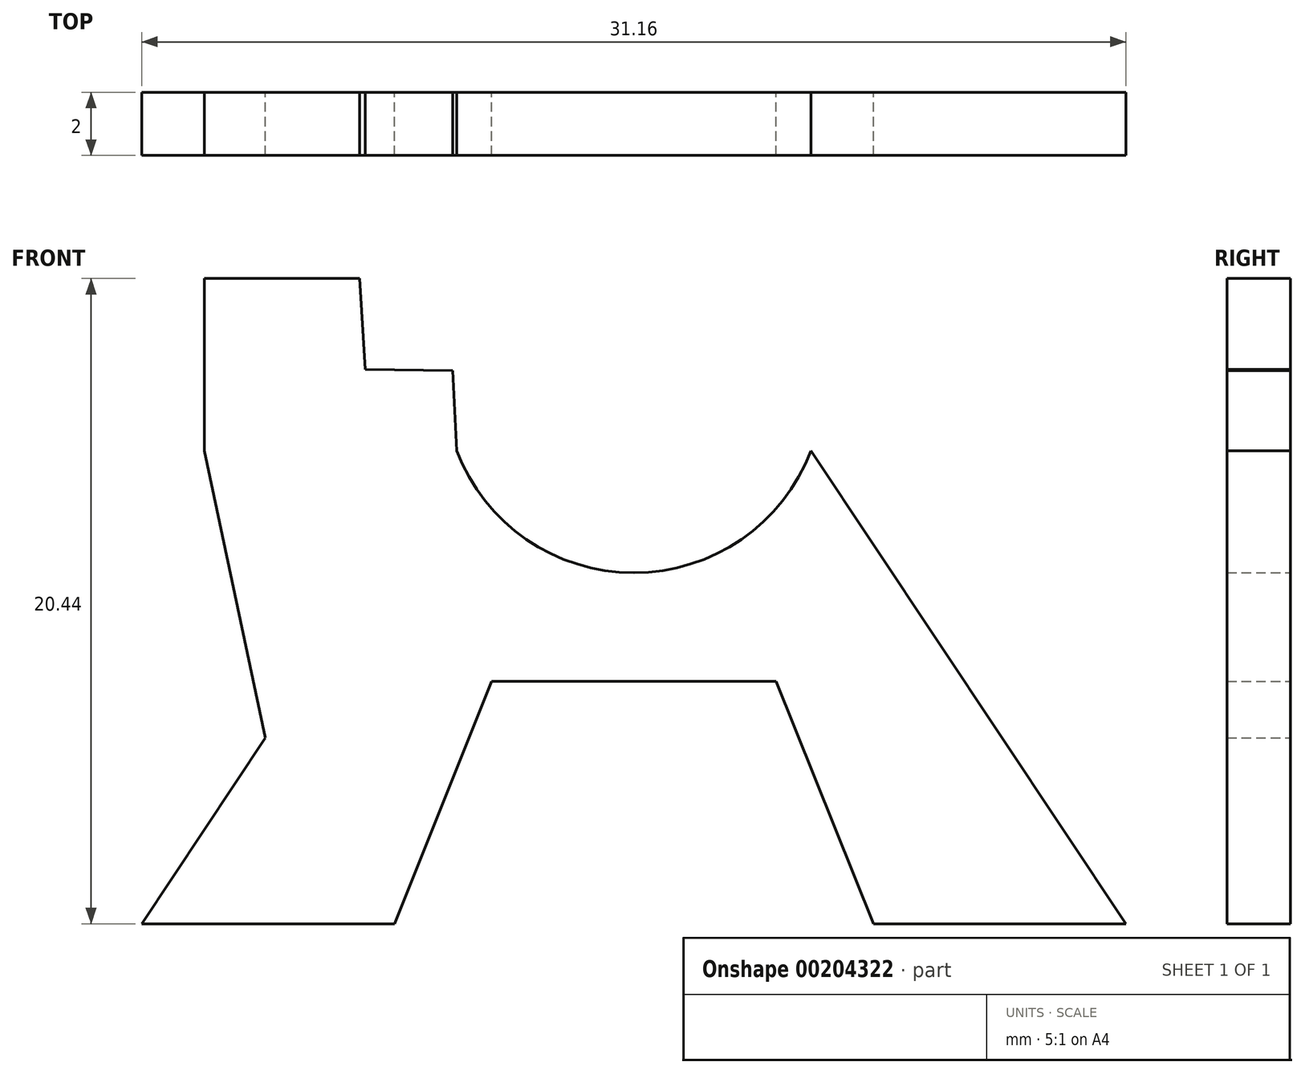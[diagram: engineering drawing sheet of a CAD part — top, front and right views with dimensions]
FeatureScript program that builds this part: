
annotation { "Feature Type Name" : "Feature", "Feature Type Description" : "" }
export const myFeature = defineFeature(function(context is Context, id is Id, definition is map)
    precondition{}
    {
        {
            var Q0;
            Q0=qCreatedBy(makeId("Front.planeOp"),FACE);
            var sketch = newSketch(context, id + "F0", { "sketchPlane" : qUnion([Q0])});
            skLineSegment(sketch, "E0", {"start": v(15.58, 0) * mm, "end": v(7.58, 0) * mm});
            skLineSegment(sketch, "E1", {"start": v(7.58, 0) * mm, "end": v(4.5, 7.68) * mm});
            skLineSegment(sketch, "E2", {"start": v(4.5, 7.68) * mm, "end": v(-4.5, 7.68) * mm});
            skLineSegment(sketch, "E3", {"start": v(-4.5, 7.68) * mm, "end": v(-7.58, 0) * mm});
            skLineSegment(sketch, "E4", {"start": v(-7.58, 0) * mm, "end": v(-15.58, 0) * mm});
            skLineSegment(sketch, "E5", {"start": v(0, 0) * mm, "end": v(0, 16.32) * mm, "construction": true});
            skArc(sketch, "E6", {"start": v(-5.6, 14.98) * mm, "mid": v(0, 11.12) * mm, "end": v(5.6, 14.98) * mm});
            skLineSegment(sketch, "E7", {"start": v(-15.58, 0) * mm, "end": v(-5.6, 14.98) * mm});
            skLineSegment(sketch, "E8", {"start": v(5.6, 14.98) * mm, "end": v(15.58, 0) * mm});
            skLineSegment(sketch, "E9", {"start": v(-13.6, 14.98) * mm, "end": v(-13.6, 20.44) * mm});
            skLineSegment(sketch, "E10", {"start": v(-13.6, 20.44) * mm, "end": v(-8.69, 20.44) * mm});
            skLineSegment(sketch, "E11", {"start": v(-8.69, 20.44) * mm, "end": v(-8.5, 17.56) * mm});
            skLineSegment(sketch, "E12", {"start": v(-8.5, 17.56) * mm, "end": v(-5.73, 17.52) * mm});
            skLineSegment(sketch, "E13", {"start": v(-5.73, 17.52) * mm, "end": v(-5.6, 14.98) * mm});
            skLineSegment(sketch, "E14", {"start": v(-13.6, 14.98) * mm, "end": v(-11.66, 5.89) * mm});
            skSolve(sketch);
        }
        {
            var Q0;
            Q0=makeQuery(id+"F0.imprint","IMPRINT",FACE,{"disambiguationData":[TD([[makeQuery(id+"F0.imprint","IMPRINT",EDGE,{"derivedFrom":sQuery(id+"F0.wireOp",EDGE,"E0")}),-1.0]])]});
            var Q1;
            Q1=makeQuery(id+"F0.imprint","IMPRINT",FACE,{"disambiguationData":[TD([[makeQuery(id+"F0.imprint","IMPRINT",EDGE,{"derivedFrom":sQuery(id+"F0.wireOp",EDGE,"E9")}),-1.0]])]});
            extrude(context, id + "F1", {"entities" : qUnion([Q0, Q1]), "depth" : 2 * mm});
        }
    });
